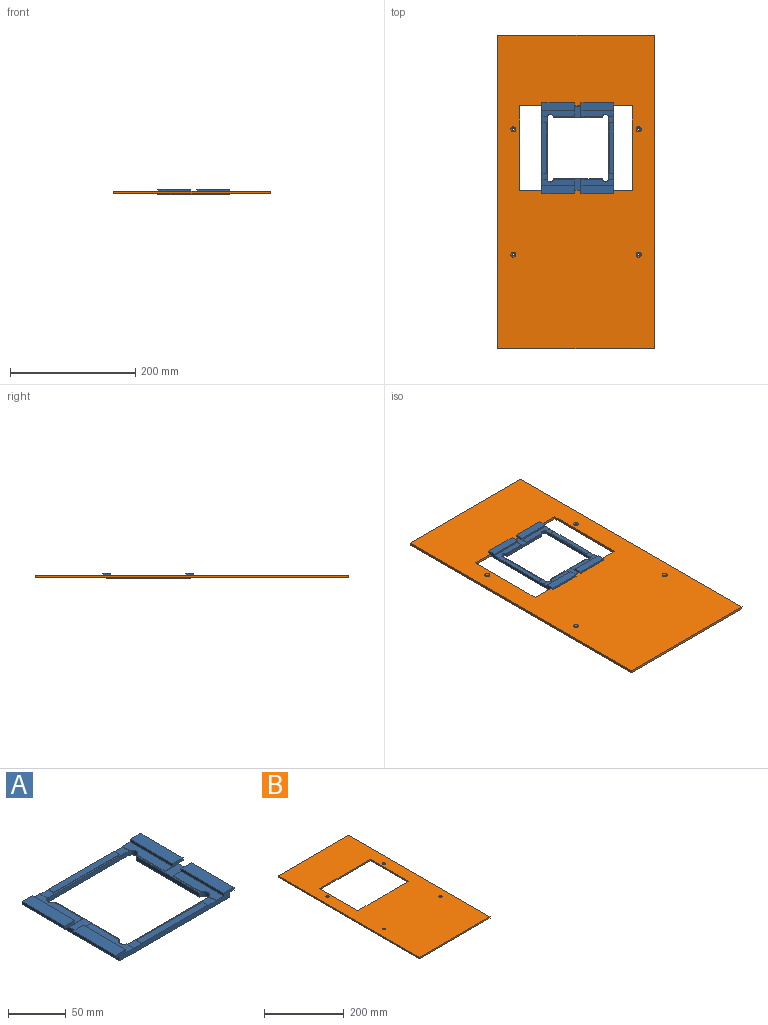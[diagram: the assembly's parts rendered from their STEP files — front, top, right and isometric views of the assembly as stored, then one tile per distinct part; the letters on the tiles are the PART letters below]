
ASSEMBLY  parts=2 mates=3
PART A: 57 faces, bbox 145x115x8 mm
  f0: plane 52.5x12.5mm, normal (0,0,1), area 656.2mm2, adj f21,f22,f31,f51
  f1: plane 52.5x12.5mm, normal (0,0,1), area 656.2mm2, adj f2,f12,f30,f55
  f2: plane 52.5x3mm, normal (1,0,0), area 157.5mm2, adj f1,f7,f12,f30
  f3: plane 52.5x3mm, normal (-1,0,0), area 157.5mm2, adj f4,f11,f12,f26
  f4: plane 52.5x12.5mm, normal (0,0,1), area 656.2mm2, adj f3,f12,f26,f54
  f5: plane 52.5x12.5mm, normal (0,0,1), area 656.2mm2, adj f22,f23,f25,f49
  f6: plane 115x5mm, normal (1,0,0), area 570mm2, adj f7,f8,f12,f13,f22,f30,f31,f32
  f7: plane 52.5x5.1mm, normal (0,0,-1), area 267.8mm2, adj f2,f6,f12,f30
  f8: plane 52.5x5.1mm, normal (0,0,-1), area 267.7mm2, adj f6,f21,f22,f31
  f9: plane 115x5mm, normal (-1,0,0), area 570mm2, adj f10,f11,f12,f13,f22,f25,f26,f27
  f10: plane 52.5x5.1mm, normal (0,0,-1), area 267.8mm2, adj f9,f22,f23,f25
  f11: plane 52.5x5.1mm, normal (0,0,-1), area 267.7mm2, adj f3,f9,f12,f26
  f12: plane 145x8mm, normal (0,-1,0), area 739mm2, adj f1,f2,f3,f4,f6,f7,f9,f11
  f13: plane 134.8x115mm, normal (0,0,-1), area 5740.9mm2, adj f6,f9,f12,f14,f15,f16,f17,f18
  f14: plane 98x4.5mm, normal (0,1,0), area 441mm2, adj f13,f15,f24,f37
  f15: cylinder r=5mm len=10mm, axis (0,0,-1), area 77mm2, adj f13,f14,f16,f27,f29,f37,f38,f53
  f16: plane 78x4.5mm, normal (1,0,0), area 351mm2, adj f13,f15,f17,f27
  f17: cylinder r=5mm len=10mm, axis (0,0,-1), area 77mm2, adj f13,f16,f18,f27,f28,f42,f43,f48
  f18: plane 98x4.5mm, normal (0,-1,0), area 441mm2, adj f13,f17,f19,f43
  f19: cylinder r=5mm len=10mm, axis (0,0,-1), area 77mm2, adj f13,f18,f20,f32,f34,f41,f43,f50
  f20: plane 78x4.5mm, normal (-1,0,0), area 351mm2, adj f13,f19,f24,f32
  f21: plane 52.5x3mm, normal (1,0,0), area 157.5mm2, adj f0,f8,f22,f31
  f22: plane 145x8mm, normal (0,1,0), area 739mm2, adj f0,f5,f6,f8,f9,f10,f13,f21
  f23: plane 52.5x3mm, normal (-1,0,0), area 157.5mm2, adj f5,f10,f22,f25
  f24: cylinder r=5mm len=10mm, axis (0,0,-1), area 77mm2, adj f13,f14,f20,f32,f33,f36,f37,f56
  f25: plane 22x3.5mm, normal (0,-1,0), area 46mm2, adj f5,f9,f10,f23,f27,f28,f48,f49
  f26: plane 22x3.5mm, normal (0,1,0), area 46mm2, adj f3,f4,f9,f11,f27,f29,f53,f54
  f27: plane 78.46x18.4mm, normal (0,0,1), area 286.2mm2, adj f9,f15,f16,f17,f25,f26,f28,f29
  f28: plane 34.23x0.5mm, normal (1,0,0), area 17.1mm2, adj f17,f25,f27,f48
  f29: plane 34.23x0.5mm, normal (1,0,0), area 17.1mm2, adj f15,f26,f27,f53
  f30: plane 22x3.5mm, normal (0,1,0), area 46mm2, adj f1,f2,f6,f7,f32,f33,f55,f56
  f31: plane 22x3.5mm, normal (0,-1,0), area 46mm2, adj f0,f6,f8,f21,f32,f34,f50,f51
  f32: plane 78.46x18.4mm, normal (0,0,1), area 286.2mm2, adj f6,f19,f20,f24,f30,f31,f33,f34
  f33: plane 34.23x0.5mm, normal (-1,0,0), area 17.1mm2, adj f24,f30,f32,f56
  f34: plane 34.23x0.5mm, normal (-1,0,0), area 17.1mm2, adj f19,f31,f32,f50
  f35: plane 81x0.5mm, normal (0,1,0), area 40.5mm2, adj f37,f39,f40,f52
  f36: plane 8.73x0.5mm, normal (-1,0,0), area 4.4mm2, adj f12,f24,f37,f56
  f37: plane 101x8.73mm, normal (0,0,1), area 291.7mm2, adj f12,f14,f15,f24,f35,f36,f38,f39
  f38: plane 8.73x0.5mm, normal (1,0,0), area 4.4mm2, adj f12,f15,f37,f53
  f39: plane 7x0.5mm, normal (1,0,0), area 3.5mm2, adj f12,f35,f37,f52
  f40: plane 7x0.5mm, normal (-1,0,0), area 3.5mm2, adj f12,f35,f37,f52
  f41: plane 8.73x0.5mm, normal (-1,0,0), area 4.4mm2, adj f19,f22,f43,f50
  f42: plane 8.73x0.5mm, normal (1,0,0), area 4.4mm2, adj f17,f22,f43,f48
  f43: plane 101x8.73mm, normal (0,0,1), area 291.7mm2, adj f17,f18,f19,f22,f41,f42,f44,f45
  f44: plane 7x0.5mm, normal (1,0,0), area 3.5mm2, adj f22,f43,f45,f47
  f45: plane 81x0.5mm, normal (0,-1,0), area 40.5mm2, adj f43,f44,f46,f47
  f46: plane 7x0.5mm, normal (-1,0,0), area 3.5mm2, adj f22,f43,f45,f47
  f47: plane 81x7mm, normal (0,0,1), area 567mm2, adj f22,f44,f45,f46
  f48: plane 52.5x9.5mm, normal (0,0,1), area 474.3mm2, adj f17,f22,f25,f28,f42,f49
  f49: plane 52.5x3mm, normal (1,0,0), area 157.5mm2, adj f5,f22,f25,f48
  f50: plane 52.5x9.5mm, normal (0,0,1), area 474.3mm2, adj f19,f22,f31,f34,f41,f51
  f51: plane 52.5x3mm, normal (-1,0,0), area 157.5mm2, adj f0,f22,f31,f50
  f52: plane 81x7mm, normal (0,0,1), area 567mm2, adj f12,f35,f39,f40
  f53: plane 52.5x9.5mm, normal (0,0,1), area 474.3mm2, adj f12,f15,f26,f29,f38,f54
  f54: plane 52.5x3mm, normal (1,0,0), area 157.5mm2, adj f4,f12,f26,f53
  f55: plane 52.5x3mm, normal (-1,0,0), area 157.5mm2, adj f1,f12,f30,f56
  f56: plane 52.5x9.5mm, normal (0,0,1), area 474.3mm2, adj f12,f24,f30,f33,f36,f55
PART B: 18 faces, bbox 250x500x4 mm
  f0: cylinder r=2.25mm len=4.5mm, axis (0,0,1), area 31.8mm2, adj f5,f17
  f1: cylinder r=2.25mm len=4.5mm, axis (0,0,1), area 31.8mm2, adj f5,f16
  f2: cylinder r=2.25mm len=4.5mm, axis (0,0,1), area 31.8mm2, adj f5,f15
  f3: cylinder r=2.25mm len=4.5mm, axis (0,0,1), area 31.8mm2, adj f5,f14
  f4: plane 500x250mm, normal (0,0,1), area 100498.9mm2, adj f6,f7,f8,f9,f10,f11,f12,f13
  f5: plane 500x250mm, normal (0,0,-1), area 100636.4mm2, adj f0,f1,f2,f3,f6,f7,f8,f9
  f6: plane 500x4mm, normal (-1,0,0), area 2000mm2, adj f4,f5,f7,f9
  f7: plane 250x4mm, normal (0,-1,0), area 1000mm2, adj f4,f5,f6,f8
  f8: plane 500x4mm, normal (1,0,0), area 2000mm2, adj f4,f5,f7,f9
  f9: plane 250x4mm, normal (0,1,0), area 1000mm2, adj f4,f5,f6,f8
  f10: plane 135x4mm, normal (-1,0,0), area 540mm2, adj f4,f5,f11,f13
  f11: plane 180x4mm, normal (0,-1,0), area 720mm2, adj f4,f5,f10,f12
  f12: plane 135x4mm, normal (1,0,0), area 540mm2, adj f4,f5,f11,f13
  f13: plane 180x4mm, normal (0,1,0), area 720mm2, adj f4,f5,f10,f12
  f14: cone r=2.25mm half-angle=45deg, axis (0,0,1), area 48.6mm2, adj f3,f4
  f15: cone r=2.25mm half-angle=45deg, axis (0,0,1), area 48.6mm2, adj f2,f4
  f16: cone r=2.25mm half-angle=45deg, axis (0,0,1), area 48.6mm2, adj f1,f4
  f17: cone r=2.25mm half-angle=45deg, axis (0,0,1), area 48.6mm2, adj f0,f4
PLACE A rot(axis=(0,0,-1),90deg) t=(-74.61,39.12,16.93)mm
PLACE B rot(axis=(-0.1,0.24,0.97),0deg) t=(-202.51,-280.78,17.93)mm
MATE planar A.f6 <-> B.f13  axis (0,-1,0) through (-74.61,-28.28,19.41)mm
MATE parallel A.f6 <-> B.f13  axis (0,-1,0) through (-74.61,-28.28,19.41)mm
MATE planar A.f8 <-> B.f4  axis (0,0,-1) through (-43.36,-30.83,21.93)mm
